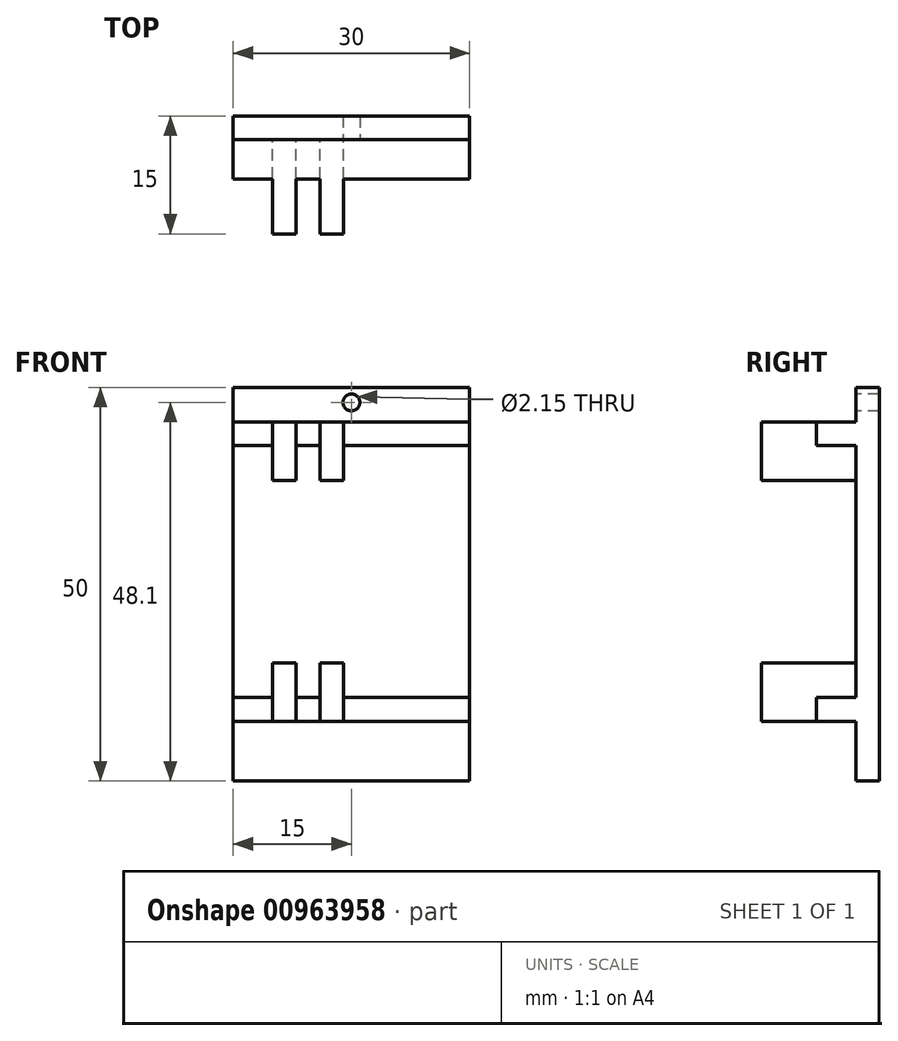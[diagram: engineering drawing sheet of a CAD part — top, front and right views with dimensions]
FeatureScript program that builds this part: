
annotation { "Feature Type Name" : "Feature", "Feature Type Description" : "" }
export const myFeature = defineFeature(function(context is Context, id is Id, definition is map)
    precondition{}
    {
        {
            var Q0;
            Q0=qCreatedBy(makeId("Top.planeOp"),FACE);
            var sketch = newSketch(context, id + "F0", { "sketchPlane" : qUnion([Q0])});
            skLineSegment(sketch, "E0.bottom", {"start": v(-15, 1.5) * mm, "end": v(15, 1.5) * mm});
            skLineSegment(sketch, "E0.top", {"start": v(-15, -1.5) * mm, "end": v(15, -1.5) * mm});
            skLineSegment(sketch, "E0.left", {"start": v(-15, 1.5) * mm, "end": v(-15, -1.5) * mm});
            skLineSegment(sketch, "E0.right", {"start": v(15, 1.5) * mm, "end": v(15, -1.5) * mm});
            skPoint(sketch, "E0.middle", {"position": v(0, 0) * mm});
            skSolve(sketch);
        }
        {
            var Q0;
            Q0=qSketchRegion(id+"F0",true);
            extrude(context, id + "F1", {"entities" : qUnion([Q0]), "endBound" : BoundingType.SYMMETRIC, "depth" : 50 * mm, "offsetDistance" : 25 * mm});
        }
        {
            var Q0;
            Q0=makeQuery(id+"F1.opExtrude","SWEPT_FACE",FACE,{"disambiguationData":[OSD([sQuery(id+"F0.wireOp",EDGE,"E0.top")])]});
            var sketch = newSketch(context, id + "F2", { "sketchPlane" : qUnion([Q0])});
            skLineSegment(sketch, "E1.bottom", {"start": v(-15, 20.6) * mm, "end": v(15, 20.6) * mm});
            skLineSegment(sketch, "E1.top", {"start": v(-15, 17.6) * mm, "end": v(15, 17.6) * mm});
            skLineSegment(sketch, "E1.left", {"start": v(-15, 20.6) * mm, "end": v(-15, 17.6) * mm});
            skLineSegment(sketch, "E1.right", {"start": v(15, 20.6) * mm, "end": v(15, 17.6) * mm});
            skLineSegment(sketch, "E2.bottom", {"start": v(-15, -14.4) * mm, "end": v(15, -14.4) * mm});
            skLineSegment(sketch, "E2.top", {"start": v(-15, -17.4) * mm, "end": v(15, -17.4) * mm});
            skLineSegment(sketch, "E2.left", {"start": v(-15, -14.4) * mm, "end": v(-15, -17.4) * mm});
            skLineSegment(sketch, "E2.right", {"start": v(15, -14.4) * mm, "end": v(15, -17.4) * mm});
            skSolve(sketch);
        }
        {
            var Q0;
            Q0 = qSketchRegion(id + "F2", true);
            extrude(context, id + "F3", {"entities" : qUnion([Q0]), "operationType" : NewBodyOperationType.ADD, "depth" : 5 * mm, "offsetDistance" : 25 * mm});
        }
        {
            var Q0;
            {var subQ2=sQuery(id+"F0.wireOp",EDGE,"E0.top");Q0=makeQuery(id+"F3.boolean.opBoolean","SPLIT",FACE,{"disambiguationData":[TD([makeQuery(id+"F3.opExtrude","SWEPT_FACE",FACE,{"disambiguationData":[OSD([sQuery(id+"F2.wireOp",EDGE,"E1.bottom")])]})])],"derivedFrom":makeQuery(id+"F1.opExtrude","SWEPT_FACE",FACE,{"disambiguationData":[OSD([subQ2])]})});}
            var sketch = newSketch(context, id + "F4", { "sketchPlane" : qUnion([Q0])});
            skPoint(sketch, "E3", {"position": v(0, 23.1) * mm});
            skSolve(sketch);
        }
        {
            var Q0;
            Q0=sQuery(id+"F4.wireOp",VERTEX,"E3");
            var Q1;
            Q1=makeQuery(id+"F1.opExtrude","SWEPT_BODY",BODY,{"disambiguationData":[OSD([sQuery(id+"F0.wireOp",EDGE,"E0.bottom"),sQuery(id+"F0.wireOp",EDGE,"E0.top"),sQuery(id+"F0.wireOp",EDGE,"E0.left"),sQuery(id+"F0.wireOp",EDGE,"E0.right")])]});
            hole(context, id + "F5", {"style" : HoleStyle.SIMPLE, "endStyle" : HoleEndStyle.BLIND, "standardTappedOrClearance" : lookupTablePath({ "standard" : "ISO", "engagement" : "75%", "pitch" : "0.35 mm", "size" : "M2.5", "type" : "Tapped" }), "standardBlindInLast" : lookupTablePath({ "standard" : "ISO", "fit" : "Normal", "engagement" : "75%", "pitch" : "0.35 mm", "size" : "M2.5", "type" : "Clearance & tapped" }), "holeDiameter" : 2.15 * mm, "majorDiameter" : 2.5 * mm, "showTappedDepth" : true, "holeDepth" : 29.55 * mm, "isTappedThrough" : true, "tappedDepth" : 28.5 * mm, "tapClearance" : 3, "startFromSketch" : true, "locations" : qUnion([Q0]), "scope" : qUnion([Q1])});
        }
        {
            var Q0;
            {var subQ2=sQuery(id+"F0.wireOp",EDGE,"E0.top");Q0=makeQuery(id+"F3.boolean.opBoolean","SPLIT",FACE,{"disambiguationData":[TD([makeQuery(id+"F3.opExtrude","SWEPT_FACE",FACE,{"disambiguationData":[OSD([sQuery(id+"F2.wireOp",EDGE,"E1.top")])]})])],"derivedFrom":makeQuery(id+"F1.opExtrude","SWEPT_FACE",FACE,{"disambiguationData":[OSD([subQ2])]})});}
            var sketch = newSketch(context, id + "F6", { "sketchPlane" : qUnion([Q0])});
            skLineSegment(sketch, "E4.bottom", {"start": v(-10, 17.6) * mm, "end": v(-7, 17.6) * mm});
            skLineSegment(sketch, "E4.top", {"start": v(-10, 13.2) * mm, "end": v(-7, 13.2) * mm});
            skLineSegment(sketch, "E4.left", {"start": v(-10, 17.6) * mm, "end": v(-10, 13.2) * mm});
            skLineSegment(sketch, "E4.right", {"start": v(-7, 17.6) * mm, "end": v(-7, 13.2) * mm});
            skLineSegment(sketch, "E5.bottom", {"start": v(-4, 17.6) * mm, "end": v(-1, 17.6) * mm});
            skLineSegment(sketch, "E5.top", {"start": v(-4, 13.2) * mm, "end": v(-1, 13.2) * mm});
            skLineSegment(sketch, "E5.left", {"start": v(-4, 17.6) * mm, "end": v(-4, 13.2) * mm});
            skLineSegment(sketch, "E5.right", {"start": v(-1, 17.6) * mm, "end": v(-1, 13.2) * mm});
            skLineSegment(sketch, "E6.bottom", {"start": v(-10, -14.4) * mm, "end": v(-7, -14.4) * mm});
            skLineSegment(sketch, "E6.top", {"start": v(-10, -10) * mm, "end": v(-7, -10) * mm});
            skLineSegment(sketch, "E6.left", {"start": v(-10, -14.4) * mm, "end": v(-10, -10) * mm});
            skLineSegment(sketch, "E6.right", {"start": v(-7, -14.4) * mm, "end": v(-7, -10) * mm});
            skLineSegment(sketch, "E7.bottom", {"start": v(-4, -14.4) * mm, "end": v(-1, -14.4) * mm});
            skLineSegment(sketch, "E7.top", {"start": v(-4, -10) * mm, "end": v(-1, -10) * mm});
            skLineSegment(sketch, "E7.left", {"start": v(-4, -14.4) * mm, "end": v(-4, -10) * mm});
            skLineSegment(sketch, "E7.right", {"start": v(-1, -14.4) * mm, "end": v(-1, -10) * mm});
            skSolve(sketch);
        }
        {
            var Q0;
            Q0 = qSketchRegion(id + "F6", true);
            var Q1;
            Q1=makeQuery(id+"F3.opExtrude","CAP_FACE",FACE,{"disambiguationData":[OSD([sQuery(id+"F2.wireOp",EDGE,"E1.bottom"),sQuery(id+"F2.wireOp",EDGE,"E1.top"),sQuery(id+"F2.wireOp",EDGE,"E1.left"),sQuery(id+"F2.wireOp",EDGE,"E1.right")])],"isStart":false});
            extrude(context, id + "F7", {"entities" : qUnion([Q0]), "operationType" : NewBodyOperationType.ADD, "depth" : 12 * mm, "endBoundEntityFace" : qUnion([Q1]), "offsetDistance" : 25 * mm});
        }
        {
            var Q0;
            Q0=makeQuery(id+"F7.opExtrude","SWEPT_FACE",FACE,{"disambiguationData":[OSD([sQuery(id+"F6.wireOp",EDGE,"E4.bottom")])]});
            var sketch = newSketch(context, id + "F8", { "sketchPlane" : qUnion([Q0])});
            skLineSegment(sketch, "E8.bottom", {"start": v(-10, -13.5) * mm, "end": v(-7, -13.5) * mm});
            skLineSegment(sketch, "E8.top", {"start": v(-10, -6.5) * mm, "end": v(-7, -6.5) * mm});
            skLineSegment(sketch, "E8.left", {"start": v(-10, -13.5) * mm, "end": v(-10, -6.5) * mm});
            skLineSegment(sketch, "E8.right", {"start": v(-7, -13.5) * mm, "end": v(-7, -6.5) * mm});
            skLineSegment(sketch, "E9.bottom", {"start": v(-4, -13.5) * mm, "end": v(-1, -13.5) * mm});
            skLineSegment(sketch, "E9.top", {"start": v(-4, -6.5) * mm, "end": v(-1, -6.5) * mm});
            skLineSegment(sketch, "E9.left", {"start": v(-4, -13.5) * mm, "end": v(-4, -6.5) * mm});
            skLineSegment(sketch, "E9.right", {"start": v(-1, -13.5) * mm, "end": v(-1, -6.5) * mm});
            skSolve(sketch);
        }
        {
            var Q0;
            Q0 = qSketchRegion(id + "F8", true);
            var Q1;
            Q1=makeQuery(id+"F3.opExtrude","SWEPT_FACE",FACE,{"disambiguationData":[OSD([sQuery(id+"F2.wireOp",EDGE,"E1.bottom")])]});
            extrude(context, id + "F9", {"entities" : qUnion([Q0]), "operationType" : NewBodyOperationType.ADD, "endBound" : BoundingType.UP_TO_SURFACE, "depth" : 25 * mm, "endBoundEntityFace" : qUnion([Q1]), "offsetDistance" : 25 * mm});
        }
        {
            var Q0;
            Q0=makeQuery(id+"F7.opExtrude","SWEPT_FACE",FACE,{"disambiguationData":[OSD([sQuery(id+"F6.wireOp",EDGE,"E6.bottom")])]});
            var sketch = newSketch(context, id + "F10", { "sketchPlane" : qUnion([Q0])});
            skLineSegment(sketch, "E10.bottom", {"start": v(-10, 13.5) * mm, "end": v(-7, 13.5) * mm});
            skLineSegment(sketch, "E10.top", {"start": v(-10, 6.5) * mm, "end": v(-7, 6.5) * mm});
            skLineSegment(sketch, "E10.left", {"start": v(-10, 13.5) * mm, "end": v(-10, 6.5) * mm});
            skLineSegment(sketch, "E10.right", {"start": v(-7, 13.5) * mm, "end": v(-7, 6.5) * mm});
            skLineSegment(sketch, "E11.bottom", {"start": v(-4, 13.5) * mm, "end": v(-1, 13.5) * mm});
            skLineSegment(sketch, "E11.top", {"start": v(-4, 6.5) * mm, "end": v(-1, 6.5) * mm});
            skLineSegment(sketch, "E11.left", {"start": v(-4, 13.5) * mm, "end": v(-4, 6.5) * mm});
            skLineSegment(sketch, "E11.right", {"start": v(-1, 13.5) * mm, "end": v(-1, 6.5) * mm});
            skSolve(sketch);
        }
        {
            var Q0;
            Q0 = qSketchRegion(id + "F10", true);
            var Q1;
            Q1=makeQuery(id+"F3.opExtrude","SWEPT_FACE",FACE,{"disambiguationData":[OSD([sQuery(id+"F2.wireOp",EDGE,"E2.top")])]});
            extrude(context, id + "F11", {"entities" : qUnion([Q0]), "operationType" : NewBodyOperationType.ADD, "endBound" : BoundingType.UP_TO_SURFACE, "depth" : 25 * mm, "endBoundEntityFace" : qUnion([Q1]), "offsetDistance" : 25 * mm});
        }
    });
